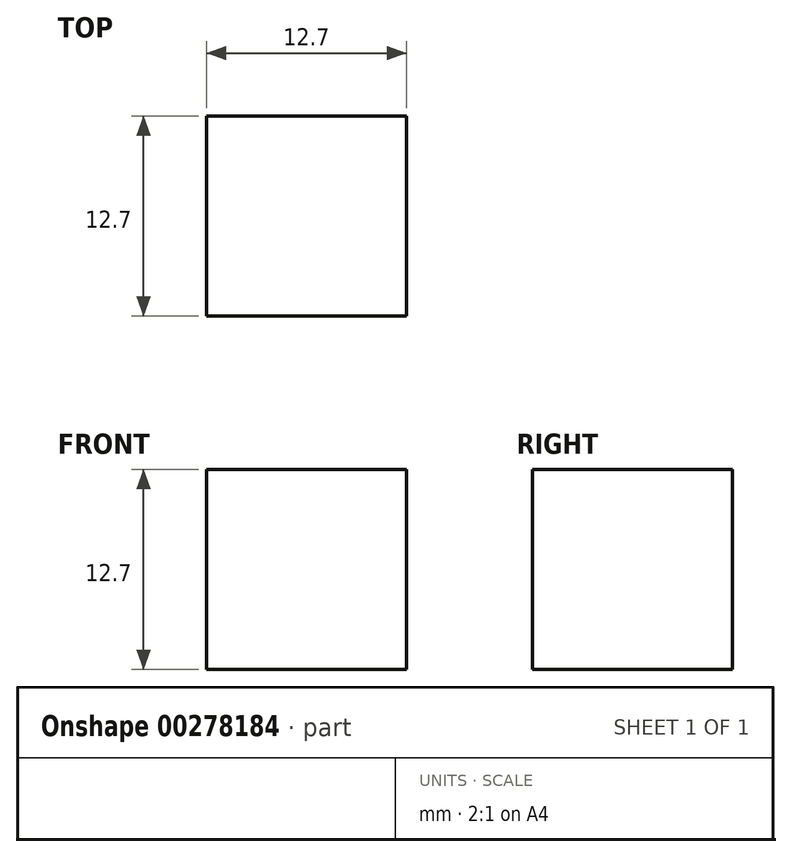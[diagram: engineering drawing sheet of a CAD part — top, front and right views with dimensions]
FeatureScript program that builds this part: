
annotation { "Feature Type Name" : "Feature", "Feature Type Description" : "" }
export const myFeature = defineFeature(function(context is Context, id is Id, definition is map)
    precondition{}
    {
        {
            var Q0;
            Q0=qCreatedBy(makeId("Top.planeOp"),FACE);
            var sketch = newSketch(context, id + "F0", { "sketchPlane" : qUnion([Q0])});
            skLineSegment(sketch, "E0.bottom", {"start": v(0, 0) * mm, "end": v(-12.7, 0) * mm});
            skLineSegment(sketch, "E0.top", {"start": v(0, 12.7) * mm, "end": v(-12.7, 12.7) * mm});
            skLineSegment(sketch, "E0.left", {"start": v(0, 0) * mm, "end": v(0, 12.7) * mm});
            skLineSegment(sketch, "E0.right", {"start": v(-12.7, 0) * mm, "end": v(-12.7, 12.7) * mm});
            skSolve(sketch);
        }
        {
            var Q0;
            Q0=makeQuery(id+"F0.imprint","IMPRINT",FACE,{"disambiguationData":[TD([[makeQuery(id+"F0.imprint","IMPRINT",EDGE,{"derivedFrom":sQuery(id+"F0.wireOp",EDGE,"E0.bottom")}),-1.0]])]});
            extrude(context, id + "F1", {"entities" : qUnion([Q0]), "depth" : 12.7 * mm});
        }
    });
